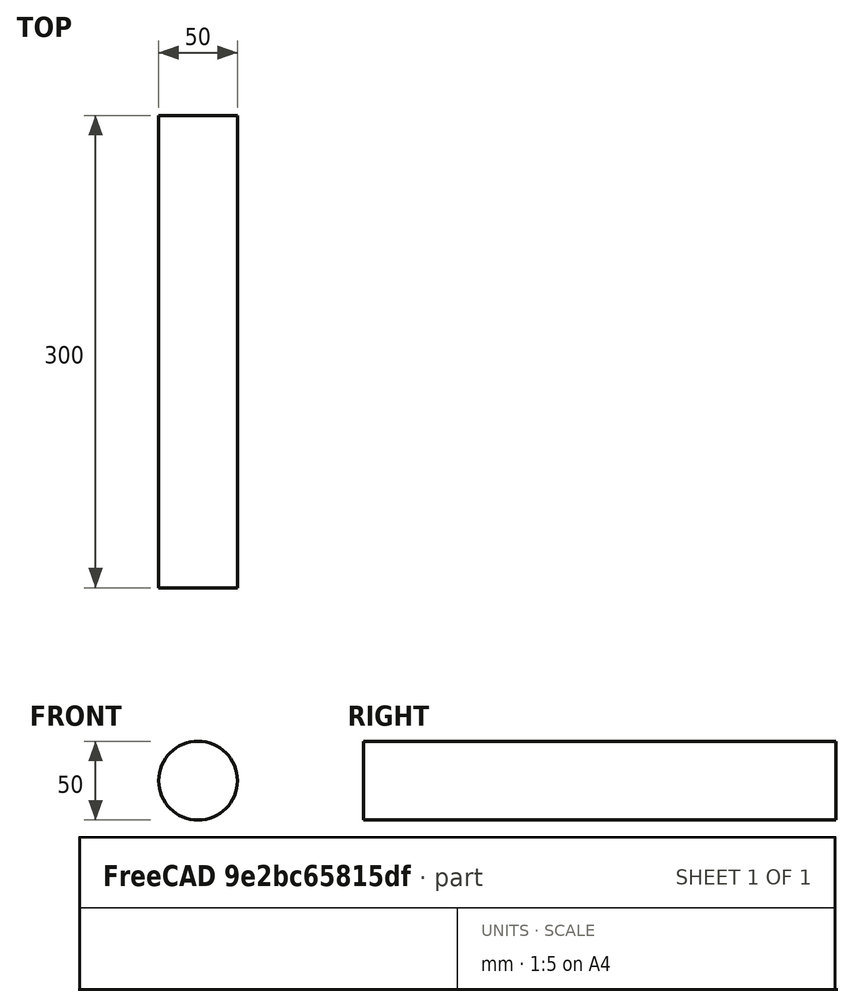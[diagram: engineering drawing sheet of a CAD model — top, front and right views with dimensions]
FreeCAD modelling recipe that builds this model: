
FCSTD DOCUMENT  (FreeCAD 0.19R24291 (Git))
Label: waterflowinCyl
License: All rights reserved
LicenseURL: http://en.wikipedia.org/wiki/All_rights_reserved
objects: Part::FeaturePython×6, App::DocumentObjectGroupPython×2, Sketcher::SketchObject×1, PartDesign::Line×1, PartDesign::Revolution×1, PartDesign::Body×1, App::MaterialObjectPython×1, Fem::FemMeshObject×1
note: 11 computed .brp shape members not serialized (recipe doc carries the construction recipe); baked Part::Feature solids carry a one-line shape summary decoded from their .brp

FEATURE [Sketcher::SketchObject] Sketch
  FullyConstrained = true
  MapMode = 5
  Placement = pos=(0,0,0) rot=(0.57735,0.57735,0.57735;2.0944rad)
  Support = -> [YZ_Plane]
  sketch-geometry (4):
    g0: LineSegment StartX=0 StartY=0 StartZ=0 EndX=300 EndY=0 EndZ=0
    g1: LineSegment StartX=0 StartY=0 StartZ=0 EndX=0 EndY=-25 EndZ=0
    g2: LineSegment StartX=0 StartY=-25 StartZ=0 EndX=300 EndY=-25 EndZ=0
    g3: LineSegment StartX=300 StartY=0 StartZ=0 EndX=300 EndY=-25 EndZ=0
  constraints (12):
    c: Coincident(g0,g-1)
    c: Distance(g0) = 300
    c: Horizontal(g0)
    c: Distance(g1) = 25
    c: Vertical(g1)
    c: Coincident(g1,g0)
    c: Horizontal(g2)
    c: Distance(g2) = 300
    c: Coincident(g2,g1)
    c: Distance(g3) = 25
    c: Vertical(g3)
    c: Coincident(g3,g0)
FEATURE [PartDesign::Line] DatumLine
  AttacherType = Attacher::AttachEngineLine
  Length = 20
  MapMode = 16
  Placement = pos=(0,0,0) rot=(0.57735,0.57735,0.57735;4.18879rad)
  ResizeMode = 0
  Support = -> [Sketch]
FEATURE [PartDesign::Revolution] Revolution
  Angle = 360
  Axis = (3e-16,1,-2e-16)
  Base = (0,0,0)
  Placement = pos=(0,0,0) rot=(0.57735,0.57735,0.57735;2.0944rad)
  Profile = -> Sketch
  ReferenceAxis = -> Sketch [H_Axis]
  Reversed = true
FEATURE [PartDesign::Body] Body
  Group = -> [Sketch,DatumLine,Revolution]
  Origin = -> Origin
  Tip = -> Revolution
FEATURE [Part::FeaturePython] PhysicsModel  # WARN: FeaturePython — macro-defined, semantics opaque (R4)
  Flow = 0
  Phase = 0
  Thermal = 0
  Time = 0
  Turbulence = 2
  TurbulenceModel = 0
  gx = 0
  gy = -9800
  gz = 0
FEATURE [App::MaterialObjectPython] FluidProperties  # material (typed FeaturePython)
  Category = 1
  Material = AuthorAndLicense=Air; CardName=Air; Cp=1004.703 J/kg/K; Density=1.20 kg/m^3; Description=Standard air properties at 20 Degrees Celsius and 1 atm; DynamicViscosity=1.80e-5 kg/m/s; MolarMass=0.0289643897748887 kg/mol; Name=Air; SutherlandRefTemperature=273.15 K; SutherlandRefViscosity=1.716e-5 kg/m/s; SutherlandTemperature=110.4 K
FEATURE [Part::FeaturePython] CfdSolver  # WARN: FeaturePython — macro-defined, semantics opaque (R4)
  ConvergenceTol = 0.0001
  EndTime = 25
  InputCaseName = case
  MaxIterations = 2000
  Parallel = true
  ParallelCores = 4
  SteadyWriteInterval = 50
  TimeStep = 0.01
  TransientWriteInterval = 1
  expr: TimeStep = 0.01s
  expr: ConvergenceTol = 0.0001
FEATURE [Part::FeaturePython] CfdFluidBoundary  label="wall"  # WARN: FeaturePython — macro-defined, semantics opaque (R4)
  BoundarySubType = 0
  BoundaryType = 0
  HeatFlux = 0
  HeatTransferCoeff = 0
  LinkedObjects = -> [Body]
  MassFlowRate = 0
  PorousBaffleMethod = 0
  Pressure = 0
  PressureDropCoeff = 0
  ReverseNormal = false
  ScreenSpacing = 2
  ScreenWireDiameter = 0.2
  SlipRatio = 0
  SpecificDissipationRate = 57
  Temperature = 290
  ThermalBoundaryType = 0
  TurbulenceInletSpecification = 0
  TurbulenceIntensity = 0.1
  TurbulenceLengthScale = 100
  TurbulentKineticEnergy = 10000
  Ux = 0
  Uy = 0
  Uz = 0
  VelocityIsCartesian = true
  VelocityMag = 0
  VolFlowRate = 0
FEATURE [Part::FeaturePython] CfdFluidBoundary001  label="inlet"  # WARN: FeaturePython — macro-defined, semantics opaque (R4)
  BoundarySubType = 7
  BoundaryType = 1
  HeatFlux = 0
  HeatTransferCoeff = 0
  LinkedObjects = -> [Body]
  MassFlowRate = 2
  PorousBaffleMethod = 0
  Pressure = 0
  PressureDropCoeff = 0
  ReverseNormal = true
  ScreenSpacing = 2
  ScreenWireDiameter = 0.2
  SlipRatio = 0
  SpecificDissipationRate = 57
  Temperature = 290
  ThermalBoundaryType = 0
  TurbulenceInletSpecification = 0
  TurbulenceIntensity = 0.1
  TurbulenceLengthScale = 100
  TurbulentKineticEnergy = 10000
  Ux = 0
  Uy = 0
  Uz = 0
  VelocityIsCartesian = true
  VelocityMag = 0
  VolFlowRate = 0
FEATURE [Part::FeaturePython] CfdFluidBoundary002  label="outlet"  # WARN: FeaturePython — macro-defined, semantics opaque (R4)
  BoundarySubType = 10
  BoundaryType = 2
  HeatFlux = 0
  HeatTransferCoeff = 0
  LinkedObjects = -> [Body]
  MassFlowRate = 0
  PorousBaffleMethod = 0
  Pressure = 0
  PressureDropCoeff = 0
  ReverseNormal = false
  ScreenSpacing = 2
  ScreenWireDiameter = 0.2
  SlipRatio = 0
  SpecificDissipationRate = 57
  Temperature = 290
  ThermalBoundaryType = 0
  TurbulenceInletSpecification = 0
  TurbulenceIntensity = 0.1
  TurbulenceLengthScale = 100
  TurbulentKineticEnergy = 10000
  Ux = 0
  Uy = 0
  Uz = 0
  VelocityIsCartesian = true
  VelocityMag = 0
  VolFlowRate = 0
FEATURE [Part::FeaturePython] InitialiseFields  # WARN: FeaturePython — macro-defined, semantics opaque (R4)
  BoundaryP = -> CfdFluidBoundary002
  BoundaryT = -> CfdFluidBoundary001
  BoundaryTurb = -> CfdFluidBoundary001
  BoundaryU = -> CfdFluidBoundary001
  PotentialFlow = false
  PotentialFlowP = false
  Pressure = 0
  Temperature = 290
  UseInletTemperatureValue = false
  UseInletTurbulenceValues = false
  UseInletUValues = false
  UseOutletPValue = true
  Ux = 25
  Uy = -5
  Uz = 10
  k = 10000
  omega = 57
FEATURE [Fem::FemMeshObject] Revolution_Mesh_Surf_Vis
FEATURE [App::DocumentObjectGroupPython] Revolution_Mesh  # scripted group (container) (typed FeaturePython)
  CaseName = meshCase
  CellsBetweenLevels = 3
  CharacteristicLengthMax = 2.5
  EdgeRefinement = 0.8
  ElementDimension = 1
  Group = -> [Revolution_Mesh_Surf_Vis]
  MeshUtility = 0
  NumberOfProcesses = 1
  NumberOfThreads = 0
  Part = -> Revolution
  PointInMesh = x=0.0 mm; y=0.0 mm; z=0.0 mm
  STLLinearDeflection = 0.05
FEATURE [App::DocumentObjectGroupPython] CfdAnalysis  # scripted group (container) (typed FeaturePython)
  Group = -> [PhysicsModel,FluidProperties,InitialiseFields,CfdSolver,Revolution_Mesh,CfdFluidBoundary,CfdFluidBoundary001,CfdFluidBoundary002]
  IsActiveAnalysis = true
